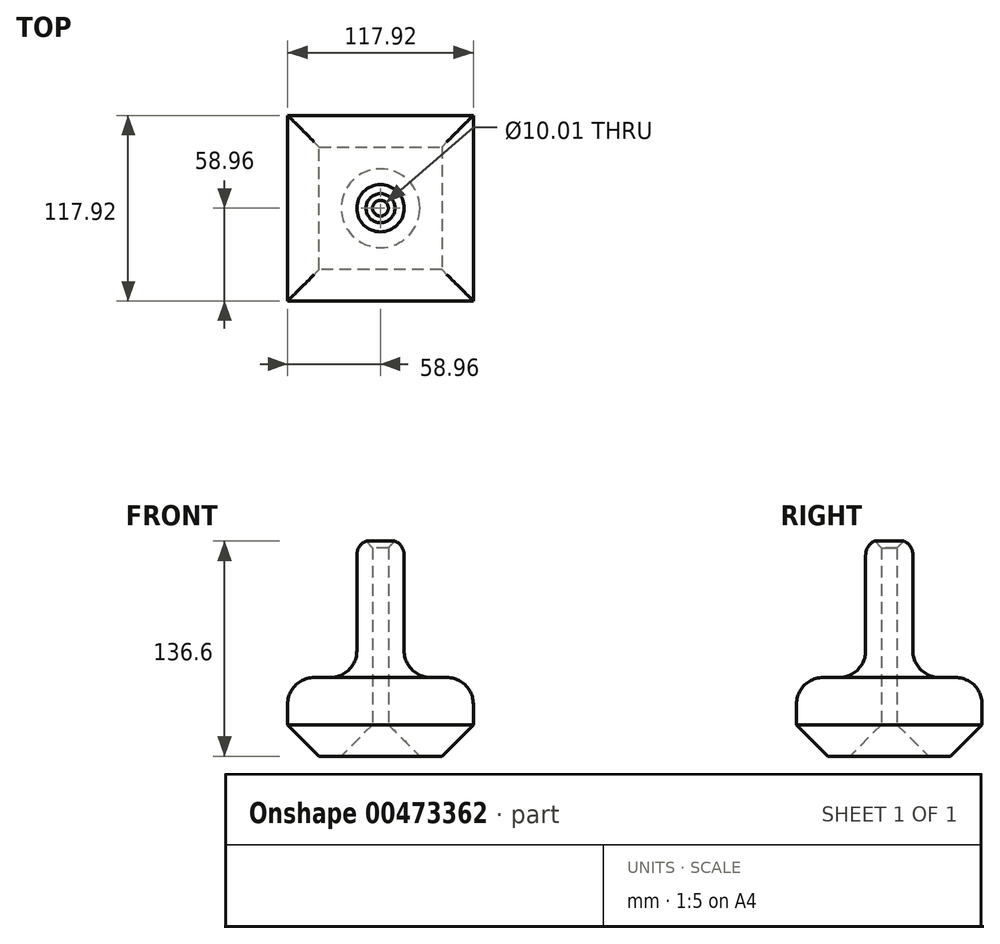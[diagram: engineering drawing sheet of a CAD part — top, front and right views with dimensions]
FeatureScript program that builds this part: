
annotation { "Feature Type Name" : "Feature", "Feature Type Description" : "" }
export const myFeature = defineFeature(function(context is Context, id is Id, definition is map)
    precondition{}
    {
        {
            var Q0;
            Q0=qCreatedBy(makeId("Top.planeOp"),FACE);
            var sketch = newSketch(context, id + "F0", { "sketchPlane" : qUnion([Q0])});
            skCircle(sketch, "E0", {"center": v(0, 0) * mm, "radius": 58.96 * mm, "construction": true});
            skLineSegment(sketch, "E1.bottom", {"start": v(-58.96, 58.96) * mm, "end": v(58.96, 58.96) * mm});
            skLineSegment(sketch, "E1.top", {"start": v(-58.96, -58.96) * mm, "end": v(58.96, -58.96) * mm});
            skLineSegment(sketch, "E1.left", {"start": v(-58.96, 58.96) * mm, "end": v(-58.96, -58.96) * mm});
            skLineSegment(sketch, "E1.right", {"start": v(58.96, 58.96) * mm, "end": v(58.96, -58.96) * mm});
            skCircle(sketch, "E2", {"center": v(0, 0) * mm, "radius": 5 * mm});
            skCircle(sketch, "E3", {"center": v(0, 0) * mm, "radius": 15.01 * mm});
            skCircle(sketch, "E4", {"center": v(10, 0) * mm, "radius": 5 * mm, "construction": true});
            skSolve(sketch);
        }
        {
            var Q0;
            Q0=makeQuery(id+"F0.imprint","IMPRINT",FACE,{"disambiguationData":[TD([[makeQuery(id+"F0.imprint","IMPRINT",EDGE,{"derivedFrom":sQuery(id+"F0.wireOp",EDGE,"E1.bottom")}),-1.0]])]});
            var Q1;
            Q1=makeQuery(id+"F0.imprint","IMPRINT",FACE,{"disambiguationData":[TD([[makeQuery(id+"F0.imprint","IMPRINT",EDGE,{"derivedFrom":sQuery(id+"F0.wireOp",EDGE,"E2")}),-1.0]])]});
            extrude(context, id + "F1", {"entities" : qUnion([Q0, Q1]), "depth" : 50 * mm});
        }
        {
            var Q0;
            Q0=makeQuery(id+"F0.imprint","IMPRINT",FACE,{"disambiguationData":[TD([[makeQuery(id+"F0.imprint","IMPRINT",EDGE,{"derivedFrom":sQuery(id+"F0.wireOp",EDGE,"E2")}),-1.0]])]});
            extrude(context, id + "F2", {"entities" : qUnion([Q0]), "operationType" : NewBodyOperationType.ADD, "depth" : 137.4 * mm});
        }
        {
            var Q0;
            Q0=makeQuery(id+"F2.opExtrude","CAP_EDGE",EDGE,{"disambiguationData":[OSD([sQuery(id+"F0.wireOp",EDGE,"E3")])],"isStart":false});
            fillet(context, id + "F3", {"entities" : qUnion([Q0]), "radius" : 9.66 * mm, "tangentPropagation" : true, "allowEdgeOverflow" : false});
        }
        {
            var Q0;
            Q0=makeQuery(id+"F2.opExtrude","CAP_EDGE",EDGE,{"disambiguationData":[OSD([sQuery(id+"F0.wireOp",EDGE,"E2")])],"isStart":false});
            chamfer(context, id + "F4", {"entities" : qUnion([Q0]), "width" : 5 * mm, "tangentPropagation" : true});
        }
        {
            var Q0;
            Q0=makeQuery(id+"F1.opExtrude","CAP_FACE",FACE,{"disambiguationData":[OSD([sQuery(id+"F0.wireOp",EDGE,"E1.bottom"),sQuery(id+"F0.wireOp",EDGE,"E1.top"),sQuery(id+"F0.wireOp",EDGE,"E1.left"),sQuery(id+"F0.wireOp",EDGE,"E1.right"),sQuery(id+"F0.wireOp",EDGE,"E2")])],"isStart":false});
            fillet(context, id + "F5", {"entities" : qUnion([Q0]), "radius" : 16.9 * mm, "tangentPropagation" : true, "allowEdgeOverflow" : false});
        }
        {
            var Q0;
            Q0=makeQuery(id+"F1.opExtrude","CAP_EDGE",EDGE,{"disambiguationData":[OSD([sQuery(id+"F0.wireOp",EDGE,"E1.left")])],"isStart":true});
            var Q1;
            Q1=makeQuery(id+"F1.opExtrude","CAP_EDGE",EDGE,{"disambiguationData":[OSD([sQuery(id+"F0.wireOp",EDGE,"E1.bottom")])],"isStart":true});
            var Q2;
            Q2=makeQuery(id+"F1.opExtrude","CAP_EDGE",EDGE,{"disambiguationData":[OSD([sQuery(id+"F0.wireOp",EDGE,"E1.right")])],"isStart":true});
            var Q3;
            Q3=makeQuery(id+"F1.opExtrude","CAP_EDGE",EDGE,{"disambiguationData":[OSD([sQuery(id+"F0.wireOp",EDGE,"E1.top")])],"isStart":true});
            var Q4;
            Q4=makeQuery(id+"F1.opExtrude","CAP_EDGE",EDGE,{"disambiguationData":[OSD([sQuery(id+"F0.wireOp",EDGE,"E2")])],"isStart":true});
            chamfer(context, id + "F6", {"entities" : qUnion([Q0, Q1, Q2, Q3, Q4]), "width" : 20 * mm, "tangentPropagation" : true});
        }
    });
